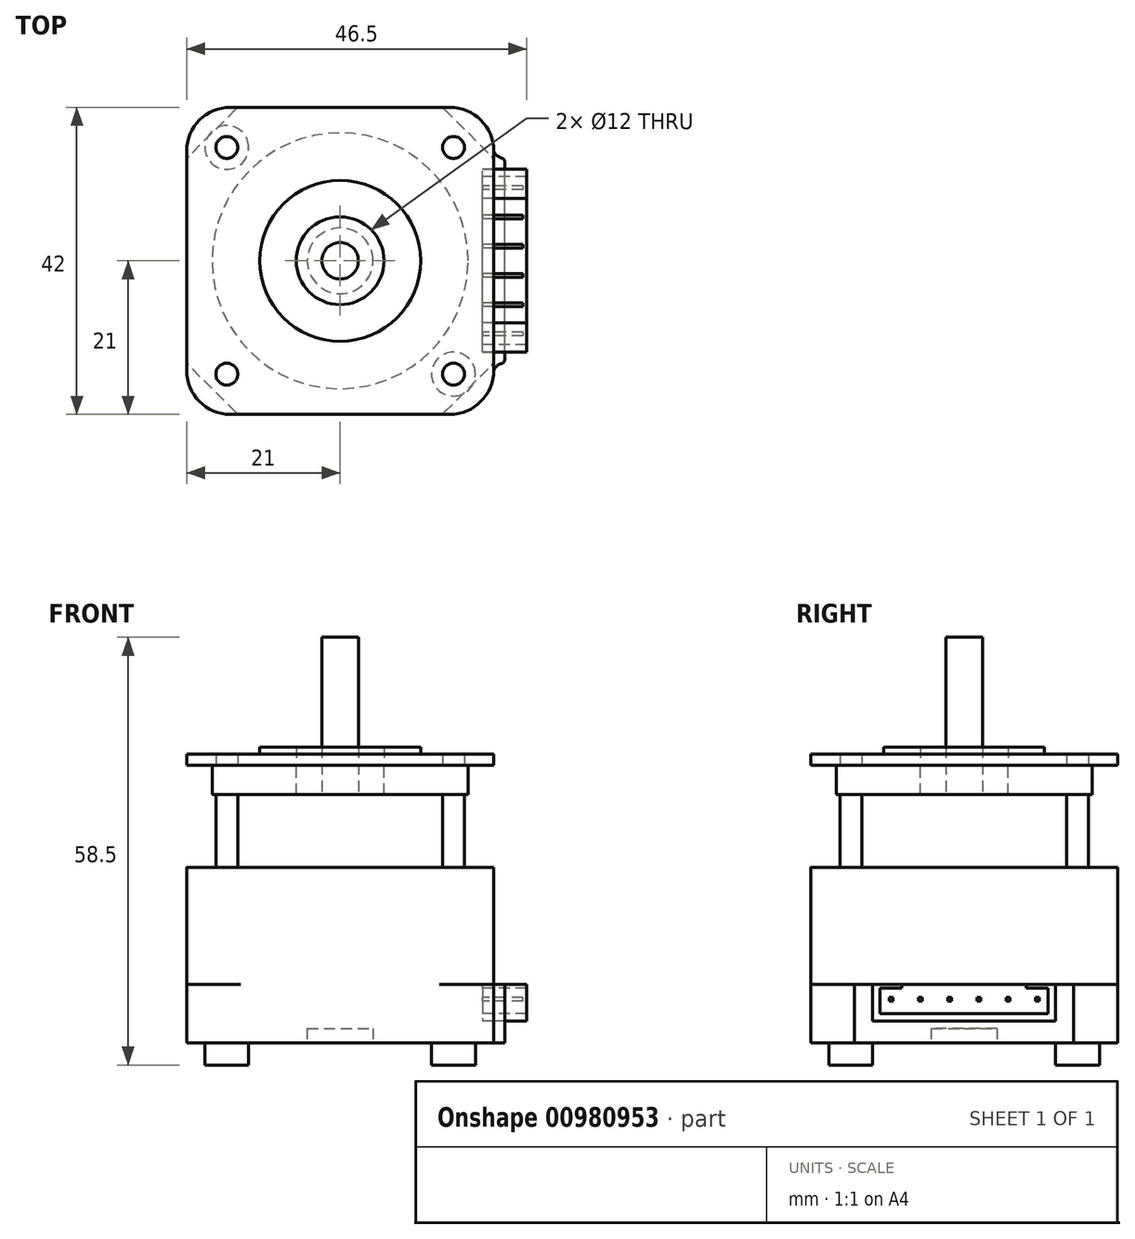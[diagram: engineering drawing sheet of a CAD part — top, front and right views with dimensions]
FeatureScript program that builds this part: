
annotation { "Feature Type Name" : "Feature", "Feature Type Description" : "" }
export const myFeature = defineFeature(function(context is Context, id is Id, definition is map)
    precondition{}
    {
        {
            var Q0;
            Q0=qCreatedBy(makeId("Top.planeOp"),FACE);
            var sketch = newSketch(context, id + "F0", { "sketchPlane" : qUnion([Q0])});
            skLineSegment(sketch, "E0.bottom", {"start": v(21, 21) * mm, "end": v(-21, 21) * mm});
            skLineSegment(sketch, "E0.top", {"start": v(21, -21) * mm, "end": v(-21, -21) * mm});
            skLineSegment(sketch, "E0.left", {"start": v(21, 21) * mm, "end": v(21, -21) * mm});
            skLineSegment(sketch, "E0.right", {"start": v(-21, 21) * mm, "end": v(-21, -21) * mm});
            skPoint(sketch, "E0.middle", {"position": v(0, 0) * mm});
            skLineSegment(sketch, "E1", {"start": v(-14, 21) * mm, "end": v(-21, 14) * mm});
            skLineSegment(sketch, "E2.MirrorCS", {"start": v(14, 21) * mm, "end": v(21, 14) * mm});
            skLineSegment(sketch, "E3.MirrorCS", {"start": v(-14, -21) * mm, "end": v(-21, -14) * mm});
            skLineSegment(sketch, "E4.MirrorCS", {"start": v(14, -21) * mm, "end": v(21, -14) * mm});
            skSolve(sketch);
        }
        {
            var Q0;
            {var subQ0=sQuery(id+"F0.wireOp",EDGE,"E1");Q0=makeQuery(id+"F0.imprint","IMPRINT",FACE,{"disambiguationData":[TD([[makeQuery(id+"F0.imprint","IMPRINT",EDGE,{"derivedFrom":subQ0}),1.0]])]});}
            extrude(context, id + "F1", {"entities" : qUnion([Q0]), "endBound" : BoundingType.SYMMETRIC, "depth" : 18 * mm, "offsetDistance" : 25 * mm});
        }
        {
            var Q0;
            Q0=makeQuery(id+"F1.opExtrude","SWEPT_EDGE",EDGE,{"disambiguationData":[OSD([sQuery(id+"F0.wireOp",EDGE,"E0.right"),sQuery(id+"F0.wireOp",EDGE,"E3.MirrorCS")])]});
            var Q1;
            Q1=makeQuery(id+"F1.opExtrude","SWEPT_EDGE",EDGE,{"disambiguationData":[OSD([sQuery(id+"F0.wireOp",EDGE,"E0.top"),sQuery(id+"F0.wireOp",EDGE,"E3.MirrorCS")])]});
            var Q2;
            Q2=makeQuery(id+"F1.opExtrude","SWEPT_EDGE",EDGE,{"disambiguationData":[OSD([sQuery(id+"F0.wireOp",EDGE,"E0.top"),sQuery(id+"F0.wireOp",EDGE,"E4.MirrorCS")])]});
            var Q3;
            Q3=makeQuery(id+"F1.opExtrude","SWEPT_EDGE",EDGE,{"disambiguationData":[OSD([sQuery(id+"F0.wireOp",EDGE,"E0.left"),sQuery(id+"F0.wireOp",EDGE,"E4.MirrorCS")])]});
            var Q4;
            Q4=makeQuery(id+"F1.opExtrude","SWEPT_EDGE",EDGE,{"disambiguationData":[OSD([sQuery(id+"F0.wireOp",EDGE,"E0.left"),sQuery(id+"F0.wireOp",EDGE,"E2.MirrorCS")])]});
            var Q5;
            Q5=makeQuery(id+"F1.opExtrude","SWEPT_EDGE",EDGE,{"disambiguationData":[OSD([sQuery(id+"F0.wireOp",EDGE,"E0.bottom"),sQuery(id+"F0.wireOp",EDGE,"E2.MirrorCS")])]});
            var Q6;
            Q6=makeQuery(id+"F1.opExtrude","SWEPT_EDGE",EDGE,{"disambiguationData":[OSD([sQuery(id+"F0.wireOp",EDGE,"E0.bottom"),sQuery(id+"F0.wireOp",EDGE,"E1")])]});
            var Q7;
            Q7=makeQuery(id+"F1.opExtrude","SWEPT_EDGE",EDGE,{"disambiguationData":[OSD([sQuery(id+"F0.wireOp",EDGE,"E0.right"),sQuery(id+"F0.wireOp",EDGE,"E1")])]});
            fillet(context, id + "F2", {"entities" : qUnion([Q0, Q1, Q2, Q3, Q4, Q5, Q6, Q7]), "radius" : 1 * mm, "tangentPropagation" : true, "defaultsChanged" : false, "vertexSettings" : [], "allowEdgeOverflow" : false});
        }
        {
            var Q0;
            Q0=makeQuery(id+"F1.opExtrude","CAP_FACE",FACE,{"disambiguationData":[OSD([sQuery(id+"F0.wireOp",EDGE,"E0.bottom"),sQuery(id+"F0.wireOp",EDGE,"E0.top"),sQuery(id+"F0.wireOp",EDGE,"E0.left"),sQuery(id+"F0.wireOp",EDGE,"E0.right"),sQuery(id+"F0.wireOp",EDGE,"E1"),sQuery(id+"F0.wireOp",EDGE,"E2.MirrorCS"),sQuery(id+"F0.wireOp",EDGE,"E3.MirrorCS"),sQuery(id+"F0.wireOp",EDGE,"E4.MirrorCS")])],"isStart":true});
            var sketch = newSketch(context, id + "F3", { "sketchPlane" : qUnion([Q0])});
            skLineSegment(sketch, "E5.bottom", {"start": v(-21, 21) * mm, "end": v(21, 21) * mm});
            skLineSegment(sketch, "E5.top", {"start": v(-21, -21) * mm, "end": v(21, -21) * mm});
            skLineSegment(sketch, "E5.left", {"start": v(-21, 21) * mm, "end": v(-21, -21) * mm});
            skLineSegment(sketch, "E5.right", {"start": v(21, 21) * mm, "end": v(21, -21) * mm});
            skPoint(sketch, "E5.middle", {"position": v(0, 0) * mm});
            skLineSegment(sketch, "E6", {"start": v(21, 14) * mm, "end": v(22.5, 14) * mm});
            skLineSegment(sketch, "E7.MirrorCS", {"start": v(21, -14) * mm, "end": v(22.5, -14) * mm});
            skLineSegment(sketch, "E8", {"start": v(22.5, 14) * mm, "end": v(22.5, -14) * mm});
            skArc(sketch, "E9", {"start": v(21, 15) * mm, "mid": v(21.6, 14.27) * mm, "end": v(22.5, 14) * mm});
            skArc(sketch, "E10.MirrorCS", {"start": v(21, -15) * mm, "mid": v(21.6, -14.27) * mm, "end": v(22.5, -14) * mm});
            skSolve(sketch);
        }
        {
            var Q0;
            {var subQ3=sQuery(id+"F0.wireOp",EDGE,"E1");Q0=makeQuery(id+"F3.imprint","IMPRINT",FACE,{"disambiguationData":[TD([[makeQuery(id+"F3.imprint","IMPRINT",EDGE,{"derivedFrom":makeQuery(id+"F1.opExtrude","CAP_EDGE",EDGE,{"disambiguationData":[OSD([subQ3])],"isStart":true})}),-1.0]])]});}
            var Q1;
            {var subQ0=sQuery(id+"F0.wireOp",EDGE,"E2.MirrorCS");Q1=makeQuery(id+"F3.imprint","IMPRINT",FACE,{"disambiguationData":[TD([[makeQuery(id+"F3.imprint","IMPRINT",EDGE,{"derivedFrom":makeQuery(id+"F1.opExtrude","CAP_EDGE",EDGE,{"disambiguationData":[OSD([subQ0])],"isStart":true})}),-1.0]])]});}
            var Q2;
            {var subQ0=sQuery(id+"F0.wireOp",EDGE,"E3.MirrorCS");Q2=makeQuery(id+"F3.imprint","IMPRINT",FACE,{"disambiguationData":[TD([[makeQuery(id+"F3.imprint","IMPRINT",EDGE,{"derivedFrom":makeQuery(id+"F1.opExtrude","CAP_EDGE",EDGE,{"disambiguationData":[OSD([subQ0])],"isStart":true})}),-1.0]])]});}
            var Q3;
            {var subQ0=sQuery(id+"F0.wireOp",EDGE,"E4.MirrorCS");Q3=makeQuery(id+"F3.imprint","IMPRINT",FACE,{"disambiguationData":[TD([[makeQuery(id+"F3.imprint","IMPRINT",EDGE,{"derivedFrom":makeQuery(id+"F1.opExtrude","CAP_EDGE",EDGE,{"disambiguationData":[OSD([subQ0])],"isStart":true})}),1.0]])]});}
            var Q4;
            {var subQ0=sQuery(id+"F0.wireOp",EDGE,"E1");Q4=makeQuery(id+"F3.imprint","IMPRINT",FACE,{"disambiguationData":[TD([[makeQuery(id+"F3.imprint","IMPRINT",EDGE,{"derivedFrom":makeQuery(id+"F1.opExtrude","CAP_EDGE",EDGE,{"disambiguationData":[OSD([subQ0])],"isStart":true})}),1.0]])]});}
            var Q5;
            {var subQ0=sQuery(id+"F3.wireOp",EDGE,"E6");Q5=makeQuery(id+"F3.imprint","IMPRINT",FACE,{"disambiguationData":[TD([[makeQuery(id+"F3.imprint","IMPRINT",EDGE,{"derivedFrom":subQ0}),-1.0]])]});}
            var Q6;
            {var subQ0=sQuery(id+"F3.wireOp",EDGE,"E6");Q6=makeQuery(id+"F3.imprint","IMPRINT",FACE,{"disambiguationData":[TD([[makeQuery(id+"F3.imprint","IMPRINT",EDGE,{"derivedFrom":subQ0}),1.0]])]});}
            var Q7;
            {var subQ0=sQuery(id+"F3.wireOp",EDGE,"E7.MirrorCS");Q7=makeQuery(id+"F3.imprint","IMPRINT",FACE,{"disambiguationData":[TD([[makeQuery(id+"F3.imprint","IMPRINT",EDGE,{"derivedFrom":subQ0}),-1.0]])]});}
            extrude(context, id + "F4", {"entities" : qUnion([Q0, Q1, Q2, Q3, Q4, Q5, Q6, Q7]), "operationType" : NewBodyOperationType.ADD, "depth" : 11 * mm, "offsetDistance" : 25 * mm});
        }
        {
            var Q0;
            Q0=makeQuery(id+"F4.opExtrude","SWEPT_EDGE",EDGE,{"disambiguationData":[OSD([sQuery(id+"F3.wireOp",EDGE,"E5.bottom"),sQuery(id+"F3.wireOp",EDGE,"E5.right")])]});
            var Q1;
            Q1=makeQuery(id+"F4.opExtrude","SWEPT_EDGE",EDGE,{"disambiguationData":[OSD([sQuery(id+"F3.wireOp",EDGE,"E5.top"),sQuery(id+"F3.wireOp",EDGE,"E5.right")])]});
            var Q2;
            Q2=makeQuery(id+"F4.opExtrude","SWEPT_EDGE",EDGE,{"disambiguationData":[OSD([sQuery(id+"F3.wireOp",EDGE,"E5.top"),sQuery(id+"F3.wireOp",EDGE,"E5.left")])]});
            var Q3;
            Q3=makeQuery(id+"F4.opExtrude","SWEPT_EDGE",EDGE,{"disambiguationData":[OSD([sQuery(id+"F3.wireOp",EDGE,"E5.bottom"),sQuery(id+"F3.wireOp",EDGE,"E5.left")])]});
            fillet(context, id + "F5", {"entities" : qUnion([Q0, Q1, Q2, Q3]), "radius" : 6 * mm, "tangentPropagation" : true, "defaultsChanged" : false, "vertexSettings" : [], "allowEdgeOverflow" : false});
        }
        {
            var Q0;
            Q0=makeQuery(id+"F4.opExtrude","SWEPT_EDGE",EDGE,{"disambiguationData":[OSD([sQuery(id+"F3.wireOp",EDGE,"E6"),sQuery(id+"F3.wireOp",EDGE,"E8"),sQuery(id+"F3.wireOp",EDGE,"E9")])]});
            var Q1;
            Q1=makeQuery(id+"F4.opExtrude","SWEPT_EDGE",EDGE,{"disambiguationData":[OSD([sQuery(id+"F3.wireOp",EDGE,"E7.MirrorCS"),sQuery(id+"F3.wireOp",EDGE,"E8"),sQuery(id+"F3.wireOp",EDGE,"E10.MirrorCS")])]});
            fillet(context, id + "F6", {"entities" : qUnion([Q0, Q1]), "radius" : 0.5 * mm, "tangentPropagation" : true, "defaultsChanged" : false, "vertexSettings" : [], "allowEdgeOverflow" : false});
        }
        {
            var Q0;
            Q0=makeQuery(id+"F4.opExtrude","CAP_FACE",FACE,{"disambiguationData":[OSD([sQuery(id+"F3.wireOp",EDGE,"E5.bottom"),sQuery(id+"F3.wireOp",EDGE,"E5.top"),sQuery(id+"F3.wireOp",EDGE,"E5.left"),sQuery(id+"F3.wireOp",EDGE,"E5.right"),sQuery(id+"F3.wireOp",EDGE,"E8"),sQuery(id+"F3.wireOp",EDGE,"E9"),sQuery(id+"F3.wireOp",EDGE,"E10.MirrorCS")])],"isStart":false});
            var sketch = newSketch(context, id + "F7", { "sketchPlane" : qUnion([Q0])});
            skCircle(sketch, "E11", {"center": v(0, 0) * mm, "radius": 4.5 * mm});
            skSolve(sketch);
        }
        {
            var Q0;
            Q0=makeQuery(id+"F7.imprint","IMPRINT",FACE,{"disambiguationData":[TD([[makeQuery(id+"F7.imprint","IMPRINT",EDGE,{"derivedFrom":sQuery(id+"F7.wireOp",EDGE,"E11")}),1.0]])]});
            extrude(context, id + "F8", {"entities" : qUnion([Q0]), "operationType" : NewBodyOperationType.REMOVE, "oppositeDirection" : true, "depth" : 5 * mm, "offsetDistance" : 25 * mm});
        }
        {
            var Q0;
            Q0=makeQuery(id+"F4.opExtrude","CAP_FACE",FACE,{"disambiguationData":[OSD([sQuery(id+"F3.wireOp",EDGE,"E5.bottom"),sQuery(id+"F3.wireOp",EDGE,"E5.top"),sQuery(id+"F3.wireOp",EDGE,"E5.left"),sQuery(id+"F3.wireOp",EDGE,"E5.right"),sQuery(id+"F3.wireOp",EDGE,"E8"),sQuery(id+"F3.wireOp",EDGE,"E9"),sQuery(id+"F3.wireOp",EDGE,"E10.MirrorCS")])],"isStart":false});
            var sketch = newSketch(context, id + "F9", { "sketchPlane" : qUnion([Q0])});
            skCircle(sketch, "E12", {"center": v(-15.5, 15.5) * mm, "radius": 3 * mm});
            skCircle(sketch, "E13.MirrorC", {"center": v(-15.5, -15.5) * mm, "radius": 3 * mm});
            skCircle(sketch, "E14.MirrorC", {"center": v(15.5, 15.5) * mm, "radius": 3 * mm});
            skCircle(sketch, "E15.MirrorC", {"center": v(15.5, -15.5) * mm, "radius": 3 * mm});
            skSolve(sketch);
        }
        {
            var Q0;
            Q0=makeQuery(id+"F9.imprint","IMPRINT",FACE,{"disambiguationData":[TD([[makeQuery(id+"F9.imprint","IMPRINT",EDGE,{"derivedFrom":sQuery(id+"F9.wireOp",EDGE,"E14.MirrorC")}),-1.0]])]});
            var Q1;
            Q1=makeQuery(id+"F9.imprint","IMPRINT",FACE,{"disambiguationData":[TD([[makeQuery(id+"F9.imprint","IMPRINT",EDGE,{"derivedFrom":sQuery(id+"F9.wireOp",EDGE,"E15.MirrorC")}),1.0]])]});
            var Q2;
            Q2=makeQuery(id+"F9.imprint","IMPRINT",FACE,{"disambiguationData":[TD([[makeQuery(id+"F9.imprint","IMPRINT",EDGE,{"derivedFrom":sQuery(id+"F9.wireOp",EDGE,"E13.MirrorC")}),-1.0]])]});
            var Q3;
            Q3=makeQuery(id+"F9.imprint","IMPRINT",FACE,{"disambiguationData":[TD([[makeQuery(id+"F9.imprint","IMPRINT",EDGE,{"derivedFrom":sQuery(id+"F9.wireOp",EDGE,"E12")}),1.0]])]});
            extrude(context, id + "F10", {"entities" : qUnion([Q0, Q1, Q2, Q3]), "operationType" : NewBodyOperationType.REMOVE, "oppositeDirection" : true, "depth" : 3 * mm, "offsetDistance" : 25 * mm});
        }
        {
            var Q0;
            Q0=makeQuery(id+"F1.opExtrude","CAP_FACE",FACE,{"disambiguationData":[OSD([sQuery(id+"F0.wireOp",EDGE,"E0.bottom"),sQuery(id+"F0.wireOp",EDGE,"E0.top"),sQuery(id+"F0.wireOp",EDGE,"E0.left"),sQuery(id+"F0.wireOp",EDGE,"E0.right"),sQuery(id+"F0.wireOp",EDGE,"E1"),sQuery(id+"F0.wireOp",EDGE,"E2.MirrorCS"),sQuery(id+"F0.wireOp",EDGE,"E3.MirrorCS"),sQuery(id+"F0.wireOp",EDGE,"E4.MirrorCS")])],"isStart":false});
            var sketch = newSketch(context, id + "F11", { "sketchPlane" : qUnion([Q0])});
            skLineSegment(sketch, "E16.bottom", {"start": v(21, -21) * mm, "end": v(-21, -21) * mm});
            skLineSegment(sketch, "E16.top", {"start": v(21, 21) * mm, "end": v(-21, 21) * mm});
            skLineSegment(sketch, "E16.left", {"start": v(21, -21) * mm, "end": v(21, 21) * mm});
            skLineSegment(sketch, "E16.right", {"start": v(-21, -21) * mm, "end": v(-21, 21) * mm});
            skPoint(sketch, "E16.middle", {"position": v(0, 0) * mm});
            skSolve(sketch);
        }
        {
            var Q0;
            {var subQ3=sQuery(id+"F0.wireOp",EDGE,"E1");Q0=makeQuery(id+"F11.imprint","IMPRINT",FACE,{"disambiguationData":[TD([[makeQuery(id+"F11.imprint","IMPRINT",EDGE,{"derivedFrom":makeQuery(id+"F1.opExtrude","CAP_EDGE",EDGE,{"disambiguationData":[OSD([subQ3])],"isStart":false})}),1.0]])]});}
            var Q1;
            {var subQ0=sQuery(id+"F0.wireOp",EDGE,"E1");Q1=makeQuery(id+"F11.imprint","IMPRINT",FACE,{"disambiguationData":[TD([[makeQuery(id+"F11.imprint","IMPRINT",EDGE,{"derivedFrom":makeQuery(id+"F1.opExtrude","CAP_EDGE",EDGE,{"disambiguationData":[OSD([subQ0])],"isStart":false})}),-1.0]])]});}
            var Q2;
            {var subQ0=sQuery(id+"F0.wireOp",EDGE,"E2.MirrorCS");Q2=makeQuery(id+"F11.imprint","IMPRINT",FACE,{"disambiguationData":[TD([[makeQuery(id+"F11.imprint","IMPRINT",EDGE,{"derivedFrom":makeQuery(id+"F1.opExtrude","CAP_EDGE",EDGE,{"disambiguationData":[OSD([subQ0])],"isStart":false})}),1.0]])]});}
            var Q3;
            {var subQ0=sQuery(id+"F0.wireOp",EDGE,"E4.MirrorCS");Q3=makeQuery(id+"F11.imprint","IMPRINT",FACE,{"disambiguationData":[TD([[makeQuery(id+"F11.imprint","IMPRINT",EDGE,{"derivedFrom":makeQuery(id+"F1.opExtrude","CAP_EDGE",EDGE,{"disambiguationData":[OSD([subQ0])],"isStart":false})}),-1.0]])]});}
            var Q4;
            {var subQ0=sQuery(id+"F0.wireOp",EDGE,"E3.MirrorCS");Q4=makeQuery(id+"F11.imprint","IMPRINT",FACE,{"disambiguationData":[TD([[makeQuery(id+"F11.imprint","IMPRINT",EDGE,{"derivedFrom":makeQuery(id+"F1.opExtrude","CAP_EDGE",EDGE,{"disambiguationData":[OSD([subQ0])],"isStart":false})}),1.0]])]});}
            extrude(context, id + "F12", {"entities" : qUnion([Q0, Q1, Q2, Q3, Q4]), "operationType" : NewBodyOperationType.ADD, "depth" : 8 * mm, "offsetDistance" : 25 * mm});
        }
        {
            var Q0;
            Q0=makeQuery(id+"F12.opExtrude","SWEPT_EDGE",EDGE,{"disambiguationData":[OSD([sQuery(id+"F11.wireOp",EDGE,"E16.bottom"),sQuery(id+"F11.wireOp",EDGE,"E16.right")])]});
            var Q1;
            Q1=makeQuery(id+"F12.opExtrude","SWEPT_EDGE",EDGE,{"disambiguationData":[OSD([sQuery(id+"F11.wireOp",EDGE,"E16.bottom"),sQuery(id+"F11.wireOp",EDGE,"E16.left")])]});
            var Q2;
            Q2=makeQuery(id+"F12.opExtrude","SWEPT_EDGE",EDGE,{"disambiguationData":[OSD([sQuery(id+"F11.wireOp",EDGE,"E16.top"),sQuery(id+"F11.wireOp",EDGE,"E16.left")])]});
            var Q3;
            Q3=makeQuery(id+"F12.opExtrude","SWEPT_EDGE",EDGE,{"disambiguationData":[OSD([sQuery(id+"F11.wireOp",EDGE,"E16.top"),sQuery(id+"F11.wireOp",EDGE,"E16.right")])]});
            fillet(context, id + "F13", {"entities" : qUnion([Q0, Q1, Q2, Q3]), "radius" : 6 * mm, "tangentPropagation" : true, "defaultsChanged" : false, "vertexSettings" : [], "allowEdgeOverflow" : false});
        }
        {
            var Q0;
            Q0=makeQuery(id+"F12.opExtrude","CAP_FACE",FACE,{"disambiguationData":[OSD([sQuery(id+"F11.wireOp",EDGE,"E16.bottom"),sQuery(id+"F11.wireOp",EDGE,"E16.top"),sQuery(id+"F11.wireOp",EDGE,"E16.left"),sQuery(id+"F11.wireOp",EDGE,"E16.right")])],"isStart":false});
            var sketch = newSketch(context, id + "F14", { "sketchPlane" : qUnion([Q0])});
            skCircle(sketch, "E17", {"center": v(-15.5, 15.5) * mm, "radius": 1.5 * mm});
            skCircle(sketch, "E18.MirrorC", {"center": v(-15.5, -15.5) * mm, "radius": 1.5 * mm});
            skCircle(sketch, "E19.MirrorC", {"center": v(15.5, 15.5) * mm, "radius": 1.5 * mm});
            skCircle(sketch, "E20.MirrorC", {"center": v(15.5, -15.5) * mm, "radius": 1.5 * mm});
            skSolve(sketch);
        }
        {
            var Q0;
            Q0=makeQuery(id+"F14.imprint","IMPRINT",FACE,{"disambiguationData":[TD([[makeQuery(id+"F14.imprint","IMPRINT",EDGE,{"derivedFrom":sQuery(id+"F14.wireOp",EDGE,"E19.MirrorC")}),-1.0]])]});
            var Q1;
            Q1=makeQuery(id+"F14.imprint","IMPRINT",FACE,{"disambiguationData":[TD([[makeQuery(id+"F14.imprint","IMPRINT",EDGE,{"derivedFrom":sQuery(id+"F14.wireOp",EDGE,"E20.MirrorC")}),1.0]])]});
            var Q2;
            Q2=makeQuery(id+"F14.imprint","IMPRINT",FACE,{"disambiguationData":[TD([[makeQuery(id+"F14.imprint","IMPRINT",EDGE,{"derivedFrom":sQuery(id+"F14.wireOp",EDGE,"E18.MirrorC")}),-1.0]])]});
            var Q3;
            Q3=makeQuery(id+"F14.imprint","IMPRINT",FACE,{"disambiguationData":[TD([[makeQuery(id+"F14.imprint","IMPRINT",EDGE,{"derivedFrom":sQuery(id+"F14.wireOp",EDGE,"E17")}),1.0]])]});
            extrude(context, id + "F15", {"entities" : qUnion([Q0, Q1, Q2, Q3]), "operationType" : NewBodyOperationType.REMOVE, "oppositeDirection" : true, "depth" : 10 * mm, "offsetDistance" : 25 * mm});
        }
        {
            var Q0;
            Q0=makeQuery(id+"F12.opExtrude","CAP_FACE",FACE,{"disambiguationData":[OSD([sQuery(id+"F11.wireOp",EDGE,"E16.bottom"),sQuery(id+"F11.wireOp",EDGE,"E16.top"),sQuery(id+"F11.wireOp",EDGE,"E16.left"),sQuery(id+"F11.wireOp",EDGE,"E16.right")])],"isStart":false});
            var sketch = newSketch(context, id + "F16", { "sketchPlane" : qUnion([Q0])});
            skCircle(sketch, "E21", {"center": v(0, 0) * mm, "radius": 17.5 * mm});
            skSolve(sketch);
        }
        {
            var Q0;
            Q0=makeQuery(id+"F16.imprint","IMPRINT",FACE,{"disambiguationData":[TD([[makeQuery(id+"F16.imprint","IMPRINT",EDGE,{"derivedFrom":sQuery(id+"F16.wireOp",EDGE,"E21")}),1.0]])]});
            extrude(context, id + "F17", {"entities" : qUnion([Q0]), "depth" : 4 * mm, "offsetDistance" : 25 * mm});
        }
        {
            var Q0;
            Q0=makeQuery(id+"F17.opExtrude","CAP_FACE",FACE,{"disambiguationData":[OSD([sQuery(id+"F16.wireOp",EDGE,"E21")])],"isStart":false});
            var sketch = newSketch(context, id + "F18", { "sketchPlane" : qUnion([Q0])});
            skCircle(sketch, "E22", {"center": v(0, 0) * mm, "radius": 6 * mm});
            skSolve(sketch);
        }
        {
            var Q0;
            Q0=makeQuery(id+"F18.imprint","IMPRINT",FACE,{"disambiguationData":[TD([[makeQuery(id+"F18.imprint","IMPRINT",EDGE,{"derivedFrom":sQuery(id+"F18.wireOp",EDGE,"E22")}),1.0]])]});
            extrude(context, id + "F19", {"entities" : qUnion([Q0]), "operationType" : NewBodyOperationType.REMOVE, "oppositeDirection" : true, "depth" : 4 * mm, "offsetDistance" : 25 * mm});
        }
        {
            var Q0;
            Q0=makeQuery(id+"F12.opExtrude","CAP_FACE",FACE,{"disambiguationData":[OSD([sQuery(id+"F11.wireOp",EDGE,"E16.bottom"),sQuery(id+"F11.wireOp",EDGE,"E16.top"),sQuery(id+"F11.wireOp",EDGE,"E16.left"),sQuery(id+"F11.wireOp",EDGE,"E16.right")])],"isStart":false});
            var sketch = newSketch(context, id + "F20", { "sketchPlane" : qUnion([Q0])});
            skCircle(sketch, "E23", {"center": v(0, 0) * mm, "radius": 2.5 * mm});
            skSolve(sketch);
        }
        {
            var Q0;
            Q0=makeQuery(id+"F20.imprint","IMPRINT",FACE,{"disambiguationData":[TD([[makeQuery(id+"F20.imprint","IMPRINT",EDGE,{"derivedFrom":sQuery(id+"F20.wireOp",EDGE,"E23")}),1.0]])]});
            extrude(context, id + "F21", {"entities" : qUnion([Q0]), "operationType" : NewBodyOperationType.ADD, "depth" : (58.5 - 37) * mm, "offsetDistance" : 25 * mm});
        }
        {
            var Q0;
            Q0=makeQuery(id+"F17.opExtrude","CAP_FACE",FACE,{"disambiguationData":[OSD([sQuery(id+"F16.wireOp",EDGE,"E21")])],"isStart":false});
            var sketch = newSketch(context, id + "F22", { "sketchPlane" : qUnion([Q0])});
            skLineSegment(sketch, "E24.bottom", {"start": v(-15, -21) * mm, "end": v(15, -21) * mm});
            skLineSegment(sketch, "E24.top", {"start": v(-15, 21) * mm, "end": v(15, 21) * mm});
            skLineSegment(sketch, "E24.left", {"start": v(-21, -15) * mm, "end": v(-21, 15) * mm});
            skLineSegment(sketch, "E24.right", {"start": v(21, -15) * mm, "end": v(21, 15) * mm});
            skPoint(sketch, "E24.middle", {"position": v(0, 0) * mm});
            skPoint(sketch, "E25.visualSharp", {"position": v(21, 21) * mm});
            skArc(sketch, "E25.filletArc", {"start": v(21, 15) * mm, "mid": v(19.24, 19.24) * mm, "end": v(15, 21) * mm});
            skPoint(sketch, "E26.visualSharp", {"position": v(21, -21) * mm});
            skArc(sketch, "E26.filletArc", {"start": v(15, -21) * mm, "mid": v(19.24, -19.24) * mm, "end": v(21, -15) * mm});
            skPoint(sketch, "E27.visualSharp", {"position": v(-21, -21) * mm});
            skArc(sketch, "E27.filletArc", {"start": v(-21, -15) * mm, "mid": v(-19.24, -19.24) * mm, "end": v(-15, -21) * mm});
            skPoint(sketch, "E28.visualSharp", {"position": v(-21, 21) * mm});
            skArc(sketch, "E28.filletArc", {"start": v(-15, 21) * mm, "mid": v(-19.24, 19.24) * mm, "end": v(-21, 15) * mm});
            skCircle(sketch, "E29", {"center": v(-15.5, 15.5) * mm, "radius": 1.5 * mm});
            skCircle(sketch, "E30.MirrorC", {"center": v(-15.5, -15.5) * mm, "radius": 1.5 * mm});
            skCircle(sketch, "E31.MirrorC", {"center": v(15.5, -15.5) * mm, "radius": 1.5 * mm});
            skCircle(sketch, "E32.MirrorC", {"center": v(15.5, 15.5) * mm, "radius": 1.5 * mm});
            skCircle(sketch, "E33", {"center": v(0, 0) * mm, "radius": 6 * mm});
            skSolve(sketch);
        }
        {
            var Q0;
            Q0=makeQuery(id+"F22.imprint","IMPRINT",FACE,{"disambiguationData":[TD([[makeQuery(id+"F22.imprint","IMPRINT",EDGE,{"derivedFrom":sQuery(id+"F22.wireOp",EDGE,"E24.bottom")}),1.0]])]});
            var Q1;
            Q1=makeQuery(id+"F22.imprint","IMPRINT",FACE,{"disambiguationData":[TD([[makeQuery(id+"F22.imprint","IMPRINT",EDGE,{"derivedFrom":sQuery(id+"F22.wireOp",EDGE,"E33")}),-1.0]])]});
            extrude(context, id + "F23", {"entities" : qUnion([Q0, Q1]), "depth" : 1.5 * mm, "offsetDistance" : 25 * mm});
        }
        {
            var Q0;
            Q0=makeQuery(id+"F23.opExtrude","CAP_FACE",FACE,{"disambiguationData":[OSD([sQuery(id+"F22.wireOp",EDGE,"E24.bottom"),sQuery(id+"F22.wireOp",EDGE,"E24.top"),sQuery(id+"F22.wireOp",EDGE,"E24.left"),sQuery(id+"F22.wireOp",EDGE,"E24.right"),sQuery(id+"F22.wireOp",EDGE,"E25.filletArc"),sQuery(id+"F22.wireOp",EDGE,"E26.filletArc"),sQuery(id+"F22.wireOp",EDGE,"E27.filletArc"),sQuery(id+"F22.wireOp",EDGE,"E28.filletArc"),sQuery(id+"F22.wireOp",EDGE,"E29"),sQuery(id+"F22.wireOp",EDGE,"E30.MirrorC"),sQuery(id+"F22.wireOp",EDGE,"E31.MirrorC"),sQuery(id+"F22.wireOp",EDGE,"E32.MirrorC"),sQuery(id+"F22.wireOp",EDGE,"E33")])],"isStart":false});
            var sketch = newSketch(context, id + "F24", { "sketchPlane" : qUnion([Q0])});
            skCircle(sketch, "E34", {"center": v(0, 0) * mm, "radius": 11 * mm});
            skCircle(sketch, "E35", {"center": v(0, 0) * mm, "radius": 6 * mm});
            skSolve(sketch);
        }
        {
            var Q0;
            Q0=makeQuery(id+"F24.imprint","IMPRINT",FACE,{"disambiguationData":[TD([[makeQuery(id+"F24.imprint","IMPRINT",EDGE,{"derivedFrom":sQuery(id+"F24.wireOp",EDGE,"E34")}),1.0]])]});
            extrude(context, id + "F25", {"entities" : qUnion([Q0]), "operationType" : NewBodyOperationType.ADD, "depth" : 1 * mm, "offsetDistance" : 25 * mm});
        }
        {
            var Q0;
            Q0=makeQuery(id+"F4.opExtrude","SWEPT_FACE",FACE,{"disambiguationData":[OSD([sQuery(id+"F3.wireOp",EDGE,"E8")])]});
            var sketch = newSketch(context, id + "F26", { "sketchPlane" : qUnion([Q0])});
            skLineSegment(sketch, "E36.bottom", {"start": v(-12.5, -9) * mm, "end": v(12.5, -9) * mm});
            skLineSegment(sketch, "E36.top", {"start": v(-12.5, -14) * mm, "end": v(12.5, -14) * mm});
            skLineSegment(sketch, "E36.left", {"start": v(-12.5, -9) * mm, "end": v(-12.5, -14) * mm});
            skLineSegment(sketch, "E36.right", {"start": v(12.5, -9) * mm, "end": v(12.5, -14) * mm});
            skSolve(sketch);
        }
        {
            var Q0;
            Q0=makeQuery(id+"F26.imprint","IMPRINT",FACE,{"disambiguationData":[TD([[makeQuery(id+"F26.imprint","IMPRINT",EDGE,{"derivedFrom":sQuery(id+"F26.wireOp",EDGE,"E36.bottom")}),-1.0]])]});
            extrude(context, id + "F27", {"entities" : qUnion([Q0]), "operationType" : NewBodyOperationType.REMOVE, "oppositeDirection" : true, "depth" : 3 * mm, "offsetDistance" : 25 * mm});
        }
        {
            var Q0;
            Q0=makeQuery(id+"F27.boolean.opBoolean","COPY",FACE,{"derivedFrom":makeQuery(id+"F27.opExtrude","CAP_FACE",FACE,{"disambiguationData":[OSD([sQuery(id+"F26.wireOp",EDGE,"E36.bottom"),sQuery(id+"F26.wireOp",EDGE,"E36.top"),sQuery(id+"F26.wireOp",EDGE,"E36.left"),sQuery(id+"F26.wireOp",EDGE,"E36.right")])],"isStart":false})});
            var sketch = newSketch(context, id + "F28", { "sketchPlane" : qUnion([Q0])});
            skLineSegment(sketch, "E37.bottom", {"start": v(-12.5, -9) * mm, "end": v(-8.5, -9) * mm});
            skLineSegment(sketch, "E37.top", {"start": v(-12.5, -14) * mm, "end": v(12.5, -14) * mm});
            skLineSegment(sketch, "E37.left", {"start": v(-12.5, -9) * mm, "end": v(-12.5, -14) * mm});
            skLineSegment(sketch, "E37.right", {"start": v(12.5, -9) * mm, "end": v(12.5, -14) * mm});
            skLineSegment(sketch, "E38.0", {"start": v(-11.5, -9.5) * mm, "end": v(-11.5, -13) * mm});
            skLineSegment(sketch, "E39.0", {"start": v(-11.5, -13) * mm, "end": v(11.5, -13) * mm});
            skLineSegment(sketch, "E40.0", {"start": v(11.5, -9.5) * mm, "end": v(11.5, -13) * mm});
            skLineSegment(sketch, "E41.0", {"start": v(-11.5, -9.5) * mm, "end": v(-8.5, -9.5) * mm});
            skLineSegment(sketch, "E42", {"start": v(-8.5, -9.5) * mm, "end": v(-8.5, -9) * mm});
            skLineSegment(sketch, "E43.MirrorCS", {"start": v(8.5, -9.5) * mm, "end": v(8.5, -9) * mm});
            skLineSegment(sketch, "E44.trimOffspring", {"start": v(8.5, -9.5) * mm, "end": v(11.5, -9.5) * mm});
            skLineSegment(sketch, "E45.trimOffspring", {"start": v(8.5, -9) * mm, "end": v(12.5, -9) * mm});
            skSolve(sketch);
        }
        {
            var Q0;
            Q0=makeQuery(id+"F28.imprint","IMPRINT",FACE,{"disambiguationData":[TD([[makeQuery(id+"F28.imprint","IMPRINT",EDGE,{"derivedFrom":sQuery(id+"F28.wireOp",EDGE,"E37.bottom")}),-1.0]])]});
            extrude(context, id + "F29", {"entities" : qUnion([Q0]), "depth" : 6 * mm, "offsetDistance" : 25 * mm});
        }
        {
            var Q0;
            Q0=makeQuery(id+"F27.boolean.opBoolean","COPY",FACE,{"derivedFrom":makeQuery(id+"F27.opExtrude","CAP_FACE",FACE,{"disambiguationData":[OSD([sQuery(id+"F26.wireOp",EDGE,"E36.bottom"),sQuery(id+"F26.wireOp",EDGE,"E36.top"),sQuery(id+"F26.wireOp",EDGE,"E36.left"),sQuery(id+"F26.wireOp",EDGE,"E36.right")])],"isStart":false})});
            var sketch = newSketch(context, id + "F30", { "sketchPlane" : qUnion([Q0])});
            skLineSegment(sketch, "E46.bottom", {"start": v(-9.75, -11.25) * mm, "end": v(-10.25, -11.25) * mm});
            skLineSegment(sketch, "E46.top", {"start": v(-9.75, -10.75) * mm, "end": v(-10.25, -10.75) * mm});
            skLineSegment(sketch, "E46.left", {"start": v(-9.75, -11.25) * mm, "end": v(-9.75, -10.75) * mm});
            skLineSegment(sketch, "E46.right", {"start": v(-10.25, -11.25) * mm, "end": v(-10.25, -10.75) * mm});
            skPoint(sketch, "E46.middle", {"position": v(-10, -11) * mm});
            skLineSegment(sketch, "E47.1.0.0", {"start": v(-5.75, -11.25) * mm, "end": v(-5.75, -10.75) * mm});
            skLineSegment(sketch, "E47.1.0.1", {"start": v(-5.75, -10.75) * mm, "end": v(-6.25, -10.75) * mm});
            skLineSegment(sketch, "E47.1.0.2", {"start": v(-6.25, -11.25) * mm, "end": v(-6.25, -10.75) * mm});
            skLineSegment(sketch, "E47.1.0.3", {"start": v(-5.75, -11.25) * mm, "end": v(-6.25, -11.25) * mm});
            skLineSegment(sketch, "E47.2.0.0", {"start": v(-1.75, -11.25) * mm, "end": v(-1.75, -10.75) * mm});
            skLineSegment(sketch, "E47.2.0.1", {"start": v(-1.75, -10.75) * mm, "end": v(-2.25, -10.75) * mm});
            skLineSegment(sketch, "E47.2.0.2", {"start": v(-2.25, -11.25) * mm, "end": v(-2.25, -10.75) * mm});
            skLineSegment(sketch, "E47.2.0.3", {"start": v(-1.75, -11.25) * mm, "end": v(-2.25, -11.25) * mm});
            skLineSegment(sketch, "E47.3.0.0", {"start": v(2.25, -11.25) * mm, "end": v(2.25, -10.75) * mm});
            skLineSegment(sketch, "E47.3.0.1", {"start": v(2.25, -10.75) * mm, "end": v(1.75, -10.75) * mm});
            skLineSegment(sketch, "E47.3.0.2", {"start": v(1.75, -11.25) * mm, "end": v(1.75, -10.75) * mm});
            skLineSegment(sketch, "E47.3.0.3", {"start": v(2.25, -11.25) * mm, "end": v(1.75, -11.25) * mm});
            skLineSegment(sketch, "E47.4.0.0", {"start": v(6.25, -11.25) * mm, "end": v(6.25, -10.75) * mm});
            skLineSegment(sketch, "E47.4.0.1", {"start": v(6.25, -10.75) * mm, "end": v(5.75, -10.75) * mm});
            skLineSegment(sketch, "E47.4.0.2", {"start": v(5.75, -11.25) * mm, "end": v(5.75, -10.75) * mm});
            skLineSegment(sketch, "E47.4.0.3", {"start": v(6.25, -11.25) * mm, "end": v(5.75, -11.25) * mm});
            skLineSegment(sketch, "E47.5.0.0", {"start": v(10.25, -11.25) * mm, "end": v(10.25, -10.75) * mm});
            skLineSegment(sketch, "E47.5.0.1", {"start": v(10.25, -10.75) * mm, "end": v(9.75, -10.75) * mm});
            skLineSegment(sketch, "E47.5.0.2", {"start": v(9.75, -11.25) * mm, "end": v(9.75, -10.75) * mm});
            skLineSegment(sketch, "E47.5.0.3", {"start": v(10.25, -11.25) * mm, "end": v(9.75, -11.25) * mm});
            skLineSegment(sketch, "E47.direction1", {"start": v(-9.75, -11.25) * mm, "end": v(-5.75, -11.25) * mm, "construction": true});
            skSolve(sketch);
        }
        {
            var Q0;
            Q0=makeQuery(id+"F30.imprint","IMPRINT",FACE,{"disambiguationData":[TD([[makeQuery(id+"F30.imprint","IMPRINT",EDGE,{"derivedFrom":sQuery(id+"F30.wireOp",EDGE,"E46.bottom")}),-1.0]])]});
            var Q1;
            Q1=makeQuery(id+"F30.imprint","IMPRINT",FACE,{"disambiguationData":[TD([[makeQuery(id+"F30.imprint","IMPRINT",EDGE,{"derivedFrom":sQuery(id+"F30.wireOp",EDGE,"E47.1.0.0")}),1.0]])]});
            var Q2;
            Q2=makeQuery(id+"F30.imprint","IMPRINT",FACE,{"disambiguationData":[TD([[makeQuery(id+"F30.imprint","IMPRINT",EDGE,{"derivedFrom":sQuery(id+"F30.wireOp",EDGE,"E47.2.0.0")}),1.0]])]});
            var Q3;
            Q3=makeQuery(id+"F30.imprint","IMPRINT",FACE,{"disambiguationData":[TD([[makeQuery(id+"F30.imprint","IMPRINT",EDGE,{"derivedFrom":sQuery(id+"F30.wireOp",EDGE,"E47.3.0.0")}),1.0]])]});
            var Q4;
            Q4=makeQuery(id+"F30.imprint","IMPRINT",FACE,{"disambiguationData":[TD([[makeQuery(id+"F30.imprint","IMPRINT",EDGE,{"derivedFrom":sQuery(id+"F30.wireOp",EDGE,"E47.4.0.0")}),1.0]])]});
            var Q5;
            Q5=makeQuery(id+"F30.imprint","IMPRINT",FACE,{"disambiguationData":[TD([[makeQuery(id+"F30.imprint","IMPRINT",EDGE,{"derivedFrom":sQuery(id+"F30.wireOp",EDGE,"E47.5.0.0")}),1.0]])]});
            extrude(context, id + "F31", {"entities" : qUnion([Q0, Q1, Q2, Q3, Q4, Q5]), "operationType" : NewBodyOperationType.ADD, "depth" : 5.5 * mm, "offsetDistance" : 25 * mm});
        }
    });
